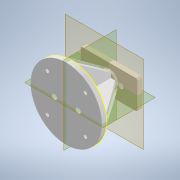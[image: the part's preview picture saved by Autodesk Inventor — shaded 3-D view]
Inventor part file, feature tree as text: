
AUTODESK INVENTOR PART (.ipt)
format: ipt  version: 2021 (Build 250183000, 183)  size: 373,248 bytes
history: native  units: mm
features: sketch x16, extrude x11, reference x6, plane x5, other x5, mirror x2, projected_geometry x2, loft x1, fillet x1
ambient origin geometry x8: Origin, YZ Plane, XZ Plane, XY Plane, X Axis, Y Axis, Z Axis, Center Point
bodies: Solid1 (feature_tree)
feature tree (49):
  extrude  "Extrusion1"  Depth=30.0mm
  extrude  "Extrusion2"  Depth=2.0mm TaperAngle=0.0deg
  sketch  "Sketch3"  dims[d6=3.0mm d7=0.0mm d8=1.4mm d9=0.0mm]
  plane  "Work Plane1"
  extrude  "Extrusion3"  Depth=1.4mm TaperAngle=0.0deg
  sketch  "Sketch4"  dims[d11=40.0mm d12=75.0mm]
  extrude  "Extrusion4"  Depth=40.0mm
  plane  "Work Plane3"
  extrude  "Extrusion5"  Depth=5.0mm TaperAngle=0.0deg
  sketch  "Sketch7"  dims[d22=8.0mm d23=38.0mm d24=0.0mm]
  sketch  "Sketch8"  dims[d26=38.0mm d27=0.0mm d28=75.0mm]
  loft  "Loft1"
  extrude  "Extrusion7"  Depth=8.0mm TaperAngle=0.0deg
  extrude  "Extrusion8"  Depth=75.0mm
  extrude  "Extrusion6"  Depth=8.0mm
  sketch  "Sketch12"  dims[d36=34.5mm d37=0.0mm d38=40.0mm d39=0.0mm]
  plane  "Work Plane4"
  extrude  "Extrusion9"  Depth=3.0mm
  plane  "Work Plane5"
  plane  "Work Plane6"
  mirror  "Mirror1"
  mirror  "Mirror2"
  sketch  "Sketch14"  dims[d43=2.0mm]
  extrude  "Extrusion10"  Depth=4.0mm
  fillet  "Fillet1"  Radius=3.0mm
  extrude  "Extrusion12"  Depth=40.0mm TaperAngle=0.0deg
  sketch  "Sketch1"  dims[d0=60.0mm d1=30.0mm]
  reference  "Reference1"
  sketch  "Sketch2"  dims[d2=2.0mm d3=0.0mm d4=3.0mm d5=0.0mm]
  reference  "Reference2"
  reference  "Reference3"
  reference  "Reference4"
  sketch  "Sketch5"  dims[d13=5.0mm d14=0.0mm d16=5.0mm d17=0.0mm]
  reference  "Reference5"
  reference  "Reference6"
  sketch  "Sketch6"  dims[d18=0.0mm d19=90.0deg d20=0.0mm d21=90.0deg]
  projected_geometry  "Projected Loop1"
  projected_geometry  "Projected Loop2"
  sketch  "Sketch9"  dims[d29=8.0mm d30=75.0mm]
  other  "Edges1"
  sketch  "Sketch10"  dims[d31=-40.0mm d32=3.0mm]
  sketch  "Sketch11"  dims[d33=4.0mm d34=4.0mm d35=3.0mm]
  sketch  "Sketch13"  dims[d40=19.0mm]
  sketch  "Sketch15"  dims[d44=10.0mm d45=0.0mm]
  sketch  "Sketch18"
  other  "539636 HGP-16-A-B-SSK---(asm_0_-ZH).iam"
  other  "539636 HGP-16-A-B-SSK---(0_1_ZYL):1"
  other  "186717 ZBH-7:2"
  other  "186717 ZBH-7:1"
